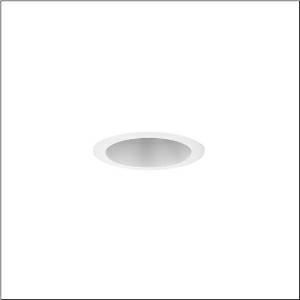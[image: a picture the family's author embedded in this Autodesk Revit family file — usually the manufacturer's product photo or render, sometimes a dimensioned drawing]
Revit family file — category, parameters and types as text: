
# Revit family: lunis_31-l_51dn15me41b
name_source: partatom
category: Lighting Fixtures
units: mm (PartAtom-declared; Revit-internal decimal feet)

## family parameters
Cut with Voids When Loaded = No
Host = Face
Light Source = No
Part Type = Normal
Room Calculation Point = No
Round Connector Dimension = Use Diameter
Shared = No

## types (1)
- --- (1 x LED, 1700 lm, 12 W, 4000K)
    Apparent Load = 12 VA
    CIE Flux Codes = 93 98 100 100 100
    Color Rendering = 80
    Color Temperature = 4000K
    Default Elevation = 1800 mm
    Description = Lunis 31, -L, downlight, light control with reflector, light emission: direct distribution, LED rated luminous flux: 1.700lm, light colour: 840, mains connection: 220..240V, AC, 50/60Hz, housing, of aluminium, white, protection rating (complete): IP20, protection rating (on room side): IP54, insulation class (complete): insulation class II (safety insulation), certification: CE, packaging unit: 1 piece
    Height = 0 mm  [stored 0 ft]
    Lamp = 1 x LED
    Lamp Light Flux = 1700 lm
    Lamp Power = 12 W
    Lamp count = 1
    Length = 188 mm  [stored 0.616798 ft]
    Luminous efficacy = 142 lm/W
    Manufacturer = Siteco
    ModVariant = No
    Model = 51DN15ME41B
    Mounting Place = Ceiling
    Mounting Type = Recessed
    Number of Poles = 1
    OnlyDefault = Yes
    Power Factor = 1
    Product Name = Lunis 31-L
    Product group = downlight
    ProductGroupID = 400
    Protection Class = Protection class II
    Protection Degree = IP 20
    RLX_Detail_Level = 1
    RLX_Emergency_Light_Flux = 0 lm
    RLX_Emergency_Type = 0
    RLX_Emergency_Type_DB = No
    RlxData = <blob elided: 22253 chars, md5=c1771533>
    Socket = socket
    Standby Power = 0 W
    System Light Flux = 1700 lm
    System Power = 12 W
    Type Comments = individual setting: luminous flux: 100 % | (OFF | ON) | 300 mA
    Type Image = l_1345911.jpg
    URL = http://relux.com
    VarID = @adj_010137
    Voltage = 0 V
    Weight = 0.00 kg
    Width = 0 mm  [stored 0 ft]

note: [stored X ft] marks values corroborated as IEEE doubles in the binary element streams (Revit-internal decimal feet)

## geometry (parser evidence)
native form markers: Blend x4, Sweep x11
no freeform markers — native parametric forms only
